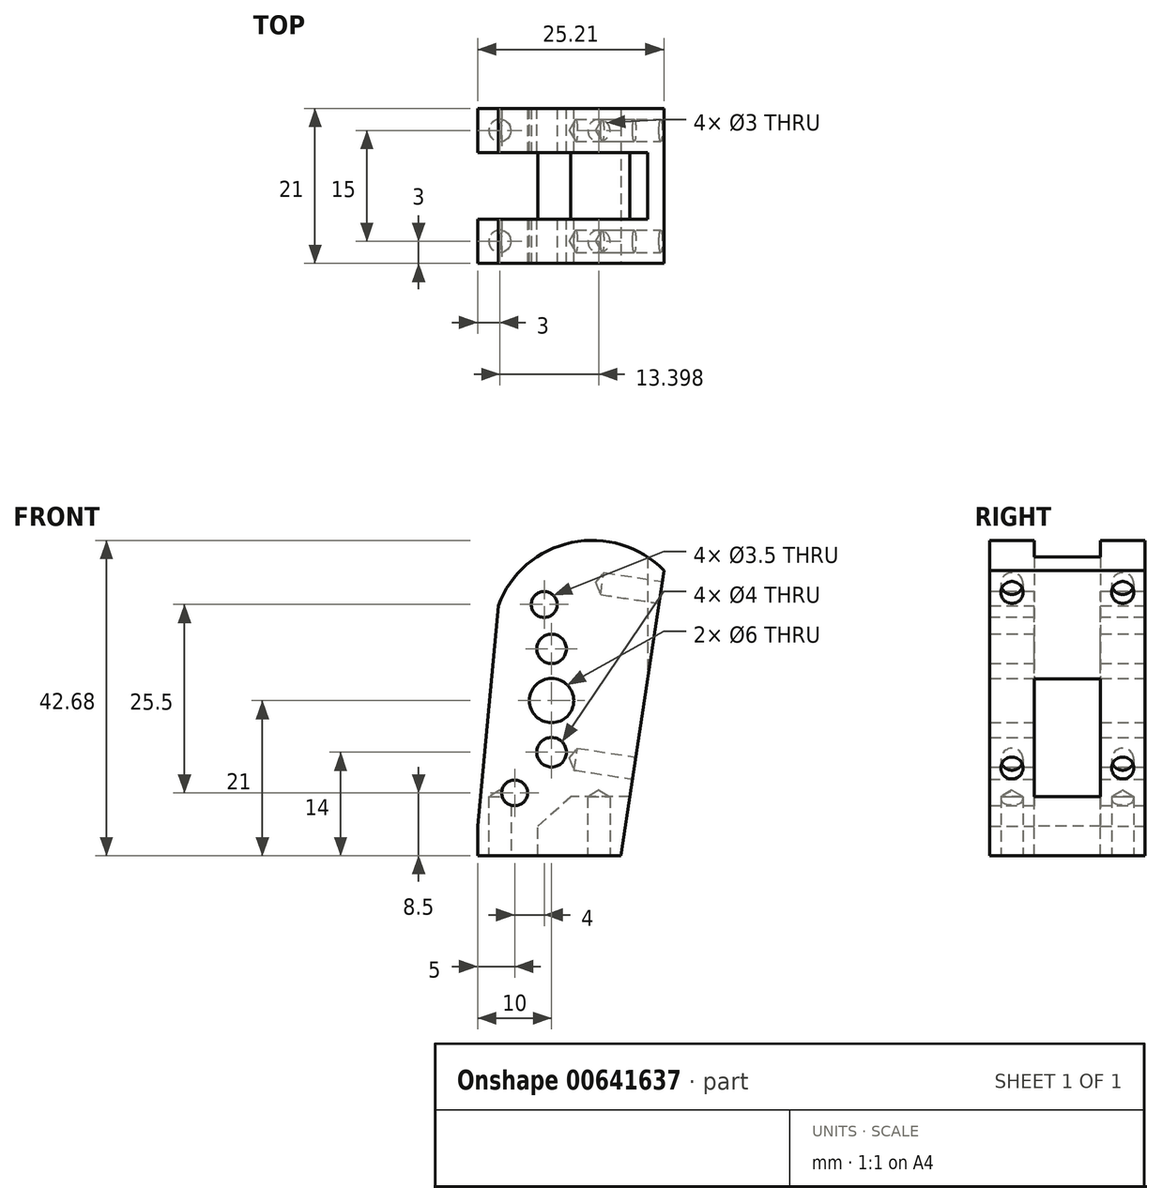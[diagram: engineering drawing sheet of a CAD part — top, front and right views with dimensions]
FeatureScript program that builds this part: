
annotation { "Feature Type Name" : "Feature", "Feature Type Description" : "" }
export const myFeature = defineFeature(function(context is Context, id is Id, definition is map)
    precondition{}
    {
        {
            var Q0;
            Q0=qCreatedBy(makeId("Front.planeOp"),FACE);
            var sketch = newSketch(context, id + "F0", { "sketchPlane" : qUnion([Q0])});
            skLineSegment(sketch, "E0", {"start": v(10, 0) * mm, "end": v(15.2, 34.61) * mm});
            skLineSegment(sketch, "E1", {"start": v(10, 0) * mm, "end": v(-10, 0) * mm});
            skLineSegment(sketch, "E2", {"start": v(-10, 0) * mm, "end": v(-7.23, 29.87) * mm});
            skArc(sketch, "E3", {"start": v(15.2, 34.61) * mm, "mid": v(2.7, 38.39) * mm, "end": v(-7.23, 29.87) * mm});
            skSolve(sketch);
        }
        {
            var Q0;
            Q0=qSketchRegion(id+"F0",true);
            extrude(context, id + "F1", {"entities" : qUnion([Q0]), "endBound" : BoundingType.SYMMETRIC, "depth" : 21 * mm, "offsetDistance" : 25 * mm});
        }
        {
            var Q0;
            Q0=qCreatedBy(makeId("Front.planeOp"),FACE);
            var sketch = newSketch(context, id + "F2", { "sketchPlane" : qUnion([Q0])});
            skLineSegment(sketch, "E4", {"start": v(13, 4) * mm, "end": v(-2, 4) * mm});
            skLineSegment(sketch, "E5", {"start": v(-2, 4) * mm, "end": v(-2.37, 0) * mm});
            skLineSegment(sketch, "E6", {"start": v(-2.37, 0) * mm, "end": v(-15, 0) * mm});
            skLineSegment(sketch, "E7", {"start": v(-15, 0) * mm, "end": v(-15, 39) * mm});
            skLineSegment(sketch, "E8", {"start": v(-15, 39) * mm, "end": v(13, 39) * mm});
            skLineSegment(sketch, "E9", {"start": v(13, 39) * mm, "end": v(13, 4) * mm});
            skSolve(sketch);
        }
        {
            var Q0;
            Q0=qSketchRegion(id+"F2",true);
            extrude(context, id + "F3", {"entities" : qUnion([Q0]), "endBound" : BoundingType.SYMMETRIC, "depth" : 9 * mm, "offsetDistance" : 25 * mm});
        }
        {
            var Q0;
            Q0=makeQuery(id+"F3.opExtrude","SWEPT_BODY",BODY,{"disambiguationData":[OSD([sQuery(id+"F2.wireOp",EDGE,"E4"),sQuery(id+"F2.wireOp",EDGE,"E5"),sQuery(id+"F2.wireOp",EDGE,"E6"),sQuery(id+"F2.wireOp",EDGE,"E7"),sQuery(id+"F2.wireOp",EDGE,"E8"),sQuery(id+"F2.wireOp",EDGE,"E9")])]});
            var Q1;
            Q1=makeQuery(id+"F1.opExtrude","SWEPT_BODY",BODY,{"disambiguationData":[OSD([sQuery(id+"F0.wireOp",EDGE,"E0"),sQuery(id+"F0.wireOp",EDGE,"E1"),sQuery(id+"F0.wireOp",EDGE,"E2"),sQuery(id+"F0.wireOp",EDGE,"wCZod6ud-FZbi-FoOU-Xc4i-ukdt4x6g0iyu")])]});
            booleanBodies(context, id + "F4", {"operationType" : BooleanOperationType.SUBTRACTION, "tools" : qUnion([Q0]), "targets" : qUnion([Q1])});
        }
        {
            var Q0;
            Q0=makeQuery(id+"F1.opExtrude","CAP_FACE",FACE,{"disambiguationData":[OSD([sQuery(id+"F0.wireOp",EDGE,"E0"),sQuery(id+"F0.wireOp",EDGE,"E1"),sQuery(id+"F0.wireOp",EDGE,"E2"),sQuery(id+"F0.wireOp",EDGE,"wCZod6ud-FZbi-FoOU-Xc4i-ukdt4x6g0iyu")])],"isStart":false});
            var sketch = newSketch(context, id + "F5", { "sketchPlane" : qUnion([Q0])});
            skLineSegment(sketch, "E10.bottom", {"start": v(-5, 4.5) * mm, "end": v(-1, 4.5) * mm});
            skLineSegment(sketch, "E10.top", {"start": v(-5, 30) * mm, "end": v(-1, 30) * mm});
            skLineSegment(sketch, "E10.left", {"start": v(-5, 4.5) * mm, "end": v(-5, 30) * mm});
            skLineSegment(sketch, "E10.right", {"start": v(-1, 4.5) * mm, "end": v(-1, 30) * mm});
            skSolve(sketch);
        }
        {
            var Q0;
            Q0=sQuery(id+"F5.wireOp",VERTEX,"E10.top.end");
            var Q1;
            Q1=sQuery(id+"F5.wireOp",VERTEX,"E10.left.start");
            var Q2;
            Q2=makeQuery(id+"F1.opExtrude","SWEPT_BODY",BODY,{"disambiguationData":[OSD([sQuery(id+"F0.wireOp",EDGE,"E0"),sQuery(id+"F0.wireOp",EDGE,"E1"),sQuery(id+"F0.wireOp",EDGE,"E2"),sQuery(id+"F0.wireOp",EDGE,"wCZod6ud-FZbi-FoOU-Xc4i-ukdt4x6g0iyu")])]});
            hole(context, id + "F6", {"style" : HoleStyle.SIMPLE, "endStyle" : HoleEndStyle.THROUGH, "holeDiameter" : 3.5 * mm, "majorDiameter" : 5 * mm, "tappedDepth" : 12 * mm, "tapClearance" : 3, "locations" : qUnion([Q0, Q1]), "scope" : qUnion([Q2])});
        }
        {
            var Q0;
            Q0=makeQuery(id+"F4.opBoolean","COPY",EDGE,{"derivedFrom":makeQuery(id+"F3.opExtrude","SWEPT_EDGE",EDGE,{"disambiguationData":[OSD([sQuery(id+"F2.wireOp",EDGE,"E4"),sQuery(id+"F2.wireOp",EDGE,"E5")])]})});
            chamfer(context, id + "F7", {"entities" : qUnion([Q0]), "width" : 5 * mm, "tangentPropagation" : true});
        }
        {
            var Q0;
            Q0=qCreatedBy(makeId("Front.planeOp"),FACE);
            var sketch = newSketch(context, id + "F8", { "sketchPlane" : qUnion([Q0])});
            skCircle(sketch, "E11", {"center": v(0, 24) * mm, "radius": 2 * mm});
            skCircle(sketch, "E12", {"center": v(0, 17) * mm, "radius": 3 * mm});
            skCircle(sketch, "E13", {"center": v(0, 10) * mm, "radius": 2 * mm});
            skSolve(sketch);
        }
        {
            var Q0;
            Q0 = qSketchRegion(id + "F8", true);
            extrude(context, id + "F9", {"entities" : qUnion([Q0]), "endBound" : BoundingType.SYMMETRIC, "depth" : 25 * mm, "offsetDistance" : 25 * mm});
        }
        {
            var Q0;
            Q0=makeQuery(id+"F9.opExtrude","SWEPT_BODY",BODY,{"disambiguationData":[OSD([sQuery(id+"F8.wireOp",EDGE,"E13")])]});
            var Q1;
            Q1=makeQuery(id+"F9.opExtrude","SWEPT_BODY",BODY,{"disambiguationData":[OSD([sQuery(id+"F8.wireOp",EDGE,"E12")])]});
            var Q2;
            Q2=makeQuery(id+"F9.opExtrude","SWEPT_BODY",BODY,{"disambiguationData":[OSD([sQuery(id+"F8.wireOp",EDGE,"E11")])]});
            var Q3;
            Q3=makeQuery(id+"F1.opExtrude","SWEPT_BODY",BODY,{"disambiguationData":[OSD([sQuery(id+"F0.wireOp",EDGE,"E0"),sQuery(id+"F0.wireOp",EDGE,"E1"),sQuery(id+"F0.wireOp",EDGE,"E2"),sQuery(id+"F0.wireOp",EDGE,"wCZod6ud-FZbi-FoOU-Xc4i-ukdt4x6g0iyu")])]});
            booleanBodies(context, id + "F10", {"operationType" : BooleanOperationType.SUBTRACTION, "tools" : qUnion([Q0, Q1, Q2]), "targets" : qUnion([Q3])});
        }
        {
            var Q0;
            Q0=makeQuery(id+"F1.opExtrude","SWEPT_FACE",FACE,{"disambiguationData":[OSD([sQuery(id+"F0.wireOp",EDGE,"E1")])]});
            extrude(context, id + "F11", {"entities" : qUnion([Q0]), "operationType" : NewBodyOperationType.ADD, "depth" : 4 * mm, "offsetDistance" : 25 * mm});
        }
        {
            var Q0;
            Q0=qCreatedBy(makeId("Front.planeOp"),FACE);
            var sketch = newSketch(context, id + "F12", { "sketchPlane" : qUnion([Q0])});
            skLineSegment(sketch, "E14", {"start": v(10, 0) * mm, "end": v(8.5, -10) * mm});
            skLineSegment(sketch, "E15", {"start": v(8.5, -10) * mm, "end": v(10, -10) * mm});
            skLineSegment(sketch, "E16", {"start": v(10, -10) * mm, "end": v(10, 0) * mm});
            skSolve(sketch);
        }
        {
            var Q0;
            Q0 = qSketchRegion(id + "F12", true);
            extrude(context, id + "F13", {"entities" : qUnion([Q0]), "endBound" : BoundingType.SYMMETRIC, "depth" : 40 * mm, "offsetDistance" : 25 * mm});
        }
        {
            var Q0;
            Q0=makeQuery(id+"F13.opExtrude","SWEPT_BODY",BODY,{"disambiguationData":[OSD([sQuery(id+"F12.wireOp",EDGE,"E14"),sQuery(id+"F12.wireOp",EDGE,"E15"),sQuery(id+"F12.wireOp",EDGE,"E16")])]});
            var Q1;
            Q1=makeQuery(id+"F1.opExtrude","SWEPT_BODY",BODY,{"disambiguationData":[OSD([sQuery(id+"F0.wireOp",EDGE,"E0"),sQuery(id+"F0.wireOp",EDGE,"E1"),sQuery(id+"F0.wireOp",EDGE,"E2"),sQuery(id+"F0.wireOp",EDGE,"E3")])]});
            booleanBodies(context, id + "F14", {"operationType" : BooleanOperationType.SUBTRACTION, "tools" : qUnion([Q0]), "targets" : qUnion([Q1])});
        }
        {
            var Q0;
            Q0=makeQuery(id+"F11.opExtrude","CAP_FACE",FACE,{"disambiguationData":[OSD([sQuery(id+"F0.wireOp",EDGE,"E1")])],"isStart":false});
            var sketch = newSketch(context, id + "F15", { "sketchPlane" : qUnion([Q0])});
            skLineSegment(sketch, "E17.bottom", {"start": v(-7, 7.5) * mm, "end": v(6.4, 7.5) * mm});
            skLineSegment(sketch, "E17.top", {"start": v(-7, -7.5) * mm, "end": v(6.4, -7.5) * mm});
            skLineSegment(sketch, "E17.left", {"start": v(-7, 7.5) * mm, "end": v(-7, -7.5) * mm});
            skLineSegment(sketch, "E17.right", {"start": v(6.4, 7.5) * mm, "end": v(6.4, -7.5) * mm});
            skSolve(sketch);
        }
        {
            var Q0;
            Q0=sQuery(id+"F15.wireOp",VERTEX,"E17.left.start");
            var Q1;
            Q1=sQuery(id+"F15.wireOp",VERTEX,"E17.right.start");
            var Q2;
            Q2=sQuery(id+"F15.wireOp",VERTEX,"E17.top.end");
            var Q3;
            Q3=sQuery(id+"F15.wireOp",VERTEX,"E17.left.end");
            var Q4;
            Q4=makeQuery(id+"F1.opExtrude","SWEPT_BODY",BODY,{"disambiguationData":[OSD([sQuery(id+"F0.wireOp",EDGE,"E0"),sQuery(id+"F0.wireOp",EDGE,"E1"),sQuery(id+"F0.wireOp",EDGE,"E2"),sQuery(id+"F0.wireOp",EDGE,"E3")])]});
            hole(context, id + "F16", {"style" : HoleStyle.SIMPLE, "endStyle" : HoleEndStyle.BLIND, "holeDiameter" : 3 * mm, "majorDiameter" : 5 * mm, "holeDepth" : 8 * mm, "tappedDepth" : 12 * mm, "tapClearance" : 3, "locations" : qUnion([Q0, Q1, Q2, Q3]), "scope" : qUnion([Q4])});
        }
        {
            var Q0;
            Q0=makeQuery(id+"F14.opBoolean","MERGE",FACE,{"derivedFrom":[makeQuery(id+"F1.opExtrude","SWEPT_FACE",FACE,{"disambiguationData":[OSD([sQuery(id+"F0.wireOp",EDGE,"E0")])]}),makeQuery(id+"F13.opExtrude","SWEPT_FACE",FACE,{"disambiguationData":[OSD([sQuery(id+"F12.wireOp",EDGE,"E14")])]})]});
            var sketch = newSketch(context, id + "F17", { "sketchPlane" : qUnion([Q0])});
            skLineSegment(sketch, "E18.bottom", {"start": v(-7.5, 33.49) * mm, "end": v(7.5, 33.49) * mm});
            skLineSegment(sketch, "E18.top", {"start": v(-7.5, 9.44) * mm, "end": v(7.5, 9.44) * mm});
            skLineSegment(sketch, "E18.left", {"start": v(-7.5, 33.49) * mm, "end": v(-7.5, 9.44) * mm});
            skLineSegment(sketch, "E18.right", {"start": v(7.5, 33.49) * mm, "end": v(7.5, 9.44) * mm});
            skSolve(sketch);
        }
        {
            var Q0;
            Q0=sQuery(id+"F17.wireOp",VERTEX,"E18.bottom.start");
            var Q1;
            Q1=sQuery(id+"F17.wireOp",VERTEX,"E18.bottom.end");
            var Q2;
            Q2=sQuery(id+"F17.wireOp",VERTEX,"E18.top.start");
            var Q3;
            Q3=sQuery(id+"F17.wireOp",VERTEX,"E18.right.end");
            var Q4;
            Q4=makeQuery(id+"F1.opExtrude","SWEPT_BODY",BODY,{"disambiguationData":[OSD([sQuery(id+"F0.wireOp",EDGE,"E0"),sQuery(id+"F0.wireOp",EDGE,"E1"),sQuery(id+"F0.wireOp",EDGE,"E2"),sQuery(id+"F0.wireOp",EDGE,"E3")])]});
            hole(context, id + "F18", {"style" : HoleStyle.SIMPLE, "endStyle" : HoleEndStyle.BLIND, "holeDiameter" : 3 * mm, "majorDiameter" : 5 * mm, "holeDepth" : 8 * mm, "tappedDepth" : 12 * mm, "tapClearance" : 3, "locations" : qUnion([Q0, Q1, Q2, Q3]), "scope" : qUnion([Q4])});
        }
    });
